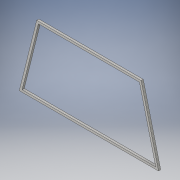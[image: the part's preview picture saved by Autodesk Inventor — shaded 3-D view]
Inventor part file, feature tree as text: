
AUTODESK INVENTOR PART (.ipt)
format: ipt  version: 2016 (Build 200138000, 138)  size: 103,936 bytes
history: native  units: in
note: dims shown in document units (in); Inventor stores cm internally (conversion verified against a paired STEP export)
features: extrude x1, sketch x1
ambient origin geometry x8: Origin, YZ Plane, XZ Plane, XY Plane, X Axis, Y Axis, Z Axis, Center Point
bodies: Solid1 (feature_tree)
feature tree (2):
  extrude  "Extrusion1"  Depth=0.125in
  sketch  "Sketch1"  dims[d0=8.0in d9=6.0in d20=0.125in d21=0.125in d24=0.125in d25=0.125in d35=4.0in d36=0.125in d37=0.0in]
